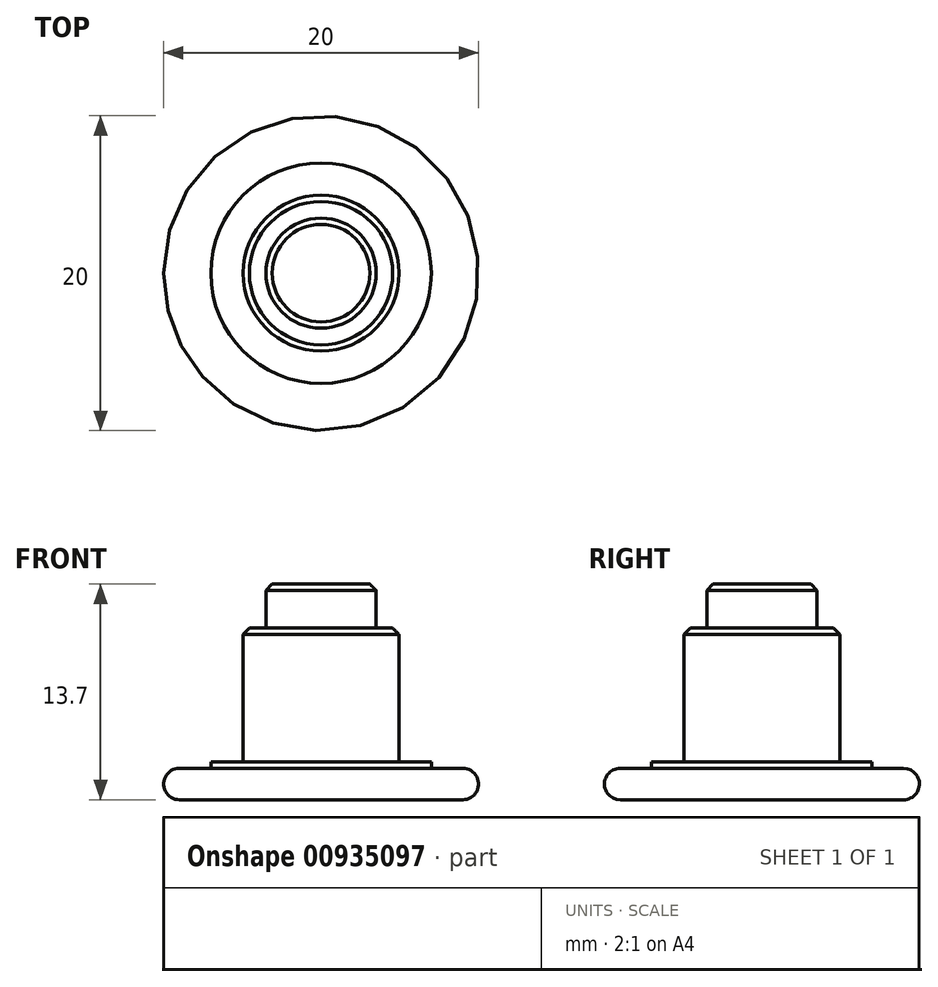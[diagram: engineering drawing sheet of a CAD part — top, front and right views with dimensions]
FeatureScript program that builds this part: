
annotation { "Feature Type Name" : "Feature", "Feature Type Description" : "" }
export const myFeature = defineFeature(function(context is Context, id is Id, definition is map)
    precondition{}
    {
        {
            var Q0;
            Q0=qCreatedBy(makeId("Top.planeOp"),FACE);
            var sketch = newSketch(context, id + "F0", { "sketchPlane" : qUnion([Q0])});
            skCircle(sketch, "E0", {"center": v(0, 0) * mm, "radius": 4.95 * mm});
            skSolve(sketch);
        }
        {
            var Q0;
            Q0 = qSketchRegion(id + "F0", true);
            extrude(context, id + "F1", {"entities" : qUnion([Q0]), "depth" : 8.5 * mm, "offsetDistance" : 25 * mm});
        }
        {
            var Q0;
            Q0=qCreatedBy(makeId("Top.planeOp"),FACE);
            var sketch = newSketch(context, id + "F2", { "sketchPlane" : qUnion([Q0])});
            skCircle(sketch, "E1", {"center": v(0, 0) * mm, "radius": 7 * mm});
            skSolve(sketch);
        }
        {
            var Q0;
            Q0 = qSketchRegion(id + "F2", true);
            extrude(context, id + "F3", {"entities" : qUnion([Q0]), "operationType" : NewBodyOperationType.ADD, "oppositeDirection" : true, "depth" : .4 * mm, "offsetDistance" : 25 * mm});
        }
        {
            var Q0;
            Q0=makeQuery(id+"F3.opExtrude","CAP_FACE",FACE,{"disambiguationData":[OSD([sQuery(id+"F2.wireOp",EDGE,"E1")])],"isStart":false});
            var sketch = newSketch(context, id + "F4", { "sketchPlane" : qUnion([Q0])});
            skCircle(sketch, "E2", {"center": v(0, 0) * mm, "radius": 10 * mm});
            skSolve(sketch);
        }
        {
            var Q0;
            Q0 = qSketchRegion(id + "F4", true);
            extrude(context, id + "F5", {"entities" : qUnion([Q0]), "operationType" : NewBodyOperationType.ADD, "depth" : 2 * mm, "offsetDistance" : 25 * mm});
        }
        {
            var Q0;
            Q0=makeQuery(id+"F5.opExtrude","CAP_EDGE",EDGE,{"disambiguationData":[OSD([sQuery(id+"F4.wireOp",EDGE,"E2")])],"isStart":false});
            var Q1;
            Q1=makeQuery(id+"F5.opExtrude","CAP_EDGE",EDGE,{"disambiguationData":[OSD([sQuery(id+"F4.wireOp",EDGE,"E2")])],"isStart":true});
            fillet(context, id + "F6", {"entities" : qUnion([Q0, Q1]), "radius" : 1 * mm, "tangentPropagation" : true, "allowEdgeOverflow" : false});
        }
        {
            var Q0;
            Q0=makeQuery(id+"F1.opExtrude","CAP_FACE",FACE,{"disambiguationData":[OSD([sQuery(id+"F0.wireOp",EDGE,"E0")])],"isStart":false});
            var sketch = newSketch(context, id + "F7", { "sketchPlane" : qUnion([Q0])});
            skCircle(sketch, "E3", {"center": v(0, 0) * mm, "radius": 3.5 * mm});
            skSolve(sketch);
        }
        {
            var Q0;
            Q0 = qSketchRegion(id + "F7", true);
            extrude(context, id + "F8", {"entities" : qUnion([Q0]), "operationType" : NewBodyOperationType.ADD, "depth" : 2.8 * mm, "offsetDistance" : 25 * mm});
        }
        {
            var Q0;
            Q0=makeQuery(id+"F8.opExtrude","CAP_EDGE",EDGE,{"disambiguationData":[OSD([sQuery(id+"F7.wireOp",EDGE,"E3")])],"isStart":false});
            var Q1;
            Q1=makeQuery(id+"F1.opExtrude","CAP_EDGE",EDGE,{"disambiguationData":[OSD([sQuery(id+"F0.wireOp",EDGE,"E0")])],"isStart":false});
            chamfer(context, id + "F9", {"entities" : qUnion([Q0, Q1]), "width" : .4 * mm, "tangentPropagation" : true});
        }
    });
